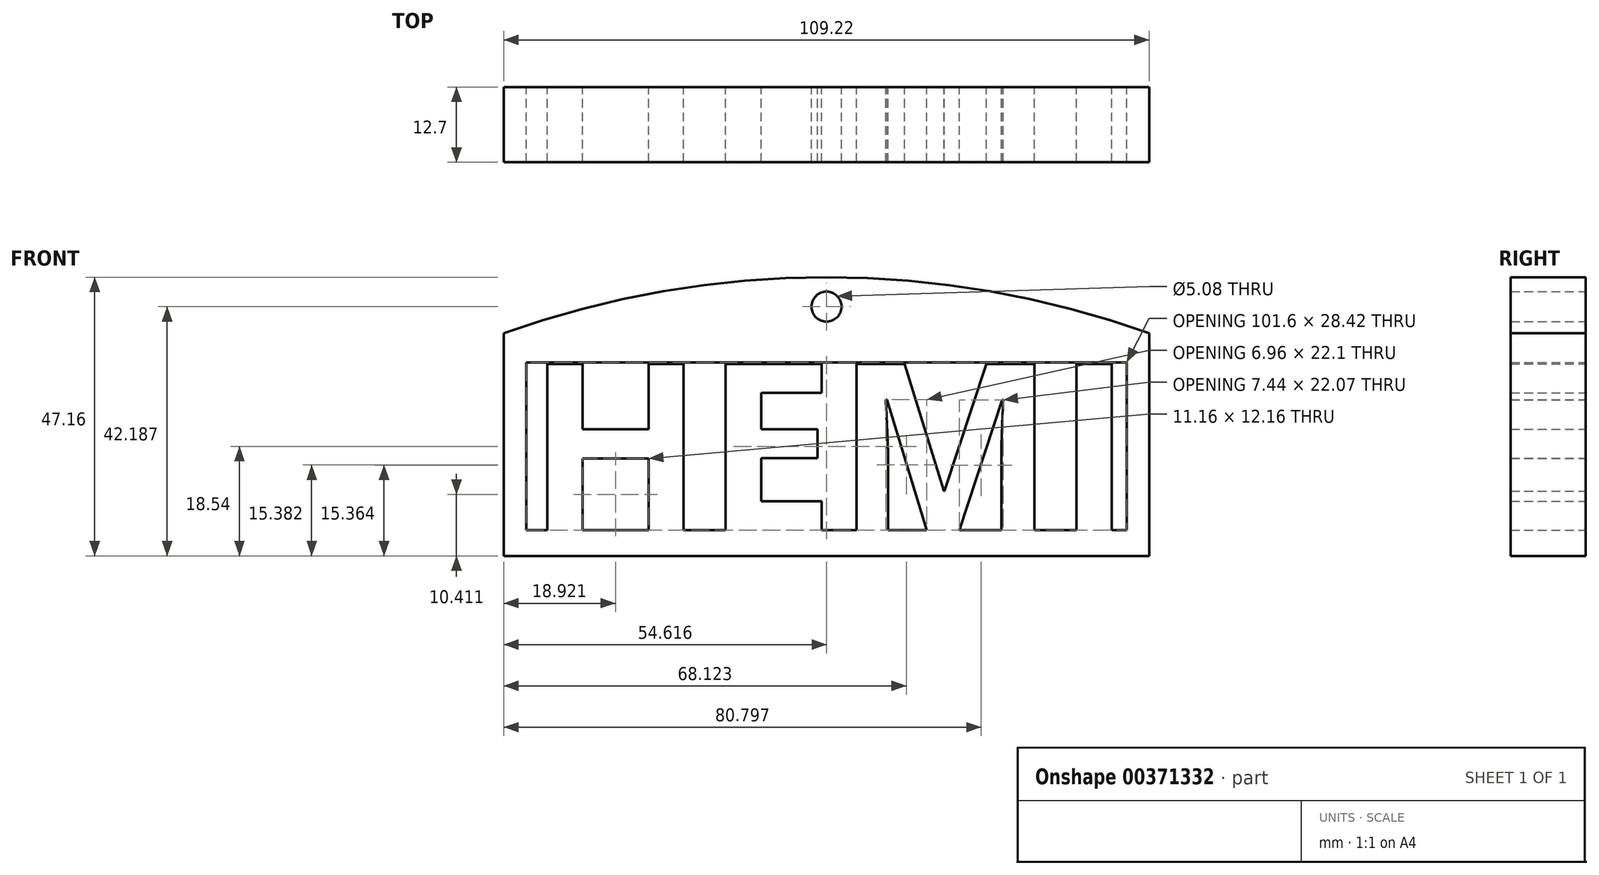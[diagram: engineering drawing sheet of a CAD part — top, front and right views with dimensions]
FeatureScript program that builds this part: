
annotation { "Feature Type Name" : "Feature", "Feature Type Description" : "" }
export const myFeature = defineFeature(function(context is Context, id is Id, definition is map)
    precondition{}
    {
        {
            var Q0;
            Q0=qCreatedBy(makeId("Front.planeOp"),FACE);
            var sketch = newSketch(context, id + "F0", { "sketchPlane" : qUnion([Q0])});
            skText(sketch, "E0", { "text": "HEMI", "fontName": "OpenSans-Bold.ttf"});
            skLineSegment(sketch, "E1", {"start": v(-25.43, 28.42) * mm, "end": v(76.17, 28.42) * mm});
            skLineSegment(sketch, "E2", {"start": v(-25.43, 28.42) * mm, "end": v(-25.43, 0) * mm});
            skLineSegment(sketch, "E3", {"start": v(-25.43, 0) * mm, "end": v(76.17, 0) * mm});
            skLineSegment(sketch, "E4", {"start": v(76.17, 0) * mm, "end": v(76.17, 28.42) * mm});
            skLineSegment(sketch, "E5.bottom", {"start": v(-29.25, -4.33) * mm, "end": v(79.97, -4.33) * mm});
            skLineSegment(sketch, "E5.top", {"start": v(-29.25, 33.37) * mm, "end": v(79.97, 33.37) * mm});
            skLineSegment(sketch, "E5.left", {"start": v(-29.25, -4.33) * mm, "end": v(-29.25, 33.37) * mm});
            skLineSegment(sketch, "E5.right", {"start": v(79.97, -4.33) * mm, "end": v(79.97, 33.37) * mm});
            skLineSegment(sketch, "E6.left", {"start": v(-29.25, 33.37) * mm, "end": v(-29.25, -4.33) * mm});
            skLineSegment(sketch, "E6.right", {"start": v(79.97, 33.37) * mm, "end": v(79.97, -4.33) * mm});
            skCircle(sketch, "E7", {"center": v(25.37, 37.86) * mm, "radius": 2.54 * mm});
            skArc(sketch, "E8", {"start": v(79.97, 33.37) * mm, "mid": v(25.36, 42.83) * mm, "end": v(-29.25, 33.37) * mm});
            const initialGuessF0  = {"E0": [-0.02543, 0, 1, 0, 0.02842]};
            skSetInitialGuess(sketch, initialGuessF0);
            skSolve(sketch);
        }
        {
            var Q0;
            {var subQ0=sQuery(id+"F0.wireOp",EDGE,"E0.sketch_text.stroke-13");Q0=makeQuery(id+"F0.imprint","IMPRINT",FACE,{"disambiguationData":[TD([[makeQuery(id+"F0.imprint","IMPRINT",EDGE,{"derivedFrom":subQ0}),-1.0]])]});}
            var Q1;
            {var subQ3=sQuery(id+"F0.wireOp",EDGE,"E0.sketch_text.stroke-24");Q1=makeQuery(id+"F0.imprint","IMPRINT",FACE,{"disambiguationData":[TD([[makeQuery(id+"F0.imprint","IMPRINT",EDGE,{"derivedFrom":subQ3}),-1.0]])]});}
            var Q2;
            {var subQ0=sQuery(id+"F0.wireOp",EDGE,"E0.sketch_text.stroke-43");Q2=makeQuery(id+"F0.imprint","IMPRINT",FACE,{"disambiguationData":[TD([[makeQuery(id+"F0.imprint","IMPRINT",EDGE,{"derivedFrom":subQ0}),-1.0]])]});}
            var Q3;
            {var subQ1=sQuery(id+"F0.wireOp",EDGE,"E0.sketch_text.stroke-1");Q3=makeQuery(id+"F0.imprint","IMPRINT",FACE,{"disambiguationData":[TD([[makeQuery(id+"F0.imprint","IMPRINT",EDGE,{"derivedFrom":subQ1}),-1.0]])]});}
            var Q4;
            Q4=makeQuery(id+"F0.imprint","IMPRINT",FACE,{"disambiguationData":[TD([[makeQuery(id+"F0.imprint","IMPRINT",EDGE,{"derivedFrom":sQuery(id+"F0.wireOp",EDGE,"E1")}),1.0]])]});
            var Q5;
            Q5=makeQuery(id+"F0.imprint","IMPRINT",FACE,{"disambiguationData":[TD([[makeQuery(id+"F0.imprint","IMPRINT",EDGE,{"derivedFrom":sQuery(id+"F0.wireOp",EDGE,"E5.top")}),1.0]])]});
            extrude(context, id + "F1", {"entities" : qUnion([Q0, Q1, Q2, Q3, Q4, Q5]), "depth" : 12.7 * mm});
        }
    });
